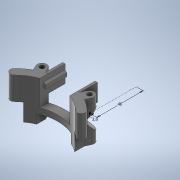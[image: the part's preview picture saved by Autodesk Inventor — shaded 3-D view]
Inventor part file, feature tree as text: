
AUTODESK INVENTOR PART (.ipt)
format: ipt  version: 2020 (Build 240168000, 168)  size: 586,240 bytes
history: native  units: mm
features: sketch x11, extrude x9, projected_geometry x7, other x2, sweep x1
ambient origin geometry x8: Origin, YZ Plane, XZ Plane, XY Plane, X Axis, Y Axis, Z Axis, Center Point
bodies: Body1 (feature_tree)
feature tree (30):
  other  "Твердое тело1"
  extrude  "Выдавливание1"  Depth=35.0mm TaperAngle=0.0deg
  sketch  "Эскиз2"
  extrude  "Выдавливание2"  Depth=4.0mm
  sweep  "Сдвиг1"
  extrude  "Выдавливание5"  Depth=8.0mm
  extrude  "Выдавливание6"  Depth=35.0mm TaperAngle=0.0deg
  extrude  "Выдавливание7"  Depth=8.5mm
  extrude  "Выдавливание8"  TaperAngle=45.0deg  [1 undecoded]
  other  "РабПлоскость1"
  extrude  "Выдавливание9"  Depth=8.5mm
  extrude  "Выдавливание10"  TaperAngle=45.0deg  [1 undecoded]
  extrude  "Выдавливание11"  TaperAngle=0.0deg  [1 undecoded]
  sketch  "Эскиз13"
  sketch  "Эскиз1"
  sketch  "Эскиз3"
  projected_geometry  "Спроецированная петля1"
  projected_geometry  "Спроецированная петля2"
  sketch  "3D эскиз1"
  sketch  "Эскиз4"
  sketch  "Эскиз6"
  projected_geometry  "Спроецированная петля4"
  sketch  "Эскиз7"
  projected_geometry  "Спроецированная петля5"
  sketch  "Эскиз9"
  projected_geometry  "Спроецированная петля7"
  sketch  "Эскиз11"
  projected_geometry  "Спроецированная петля8"
  sketch  "Эскиз12"
  projected_geometry  "Спроецированная петля9"
note: 3 required parameter values undecoded (feature->parameter linkage not recoverable at this tier; creation-order binding heuristic only, values carry confidence <= 0.55)
